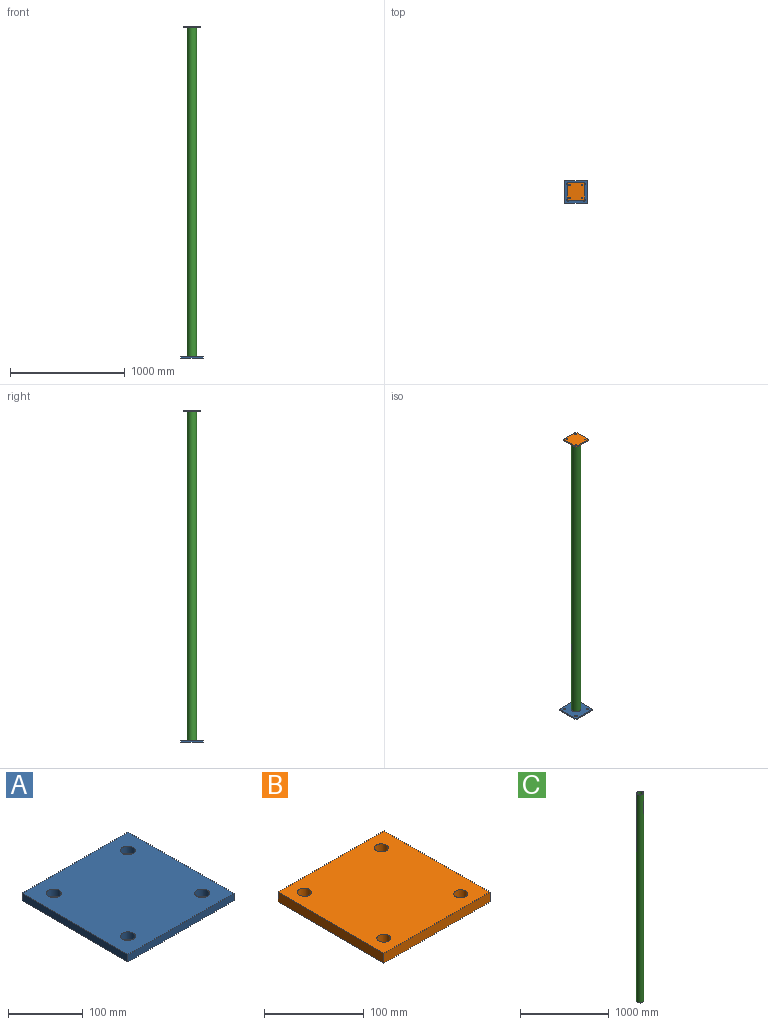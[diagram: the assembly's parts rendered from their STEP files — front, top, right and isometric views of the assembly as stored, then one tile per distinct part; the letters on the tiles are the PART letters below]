
ASSEMBLY  parts=3 mates=2
PART A: 10 faces, bbox 200x200x12 mm
  f0: plane 200x12mm, normal (0,-1,0), area 2400mm2, adj f1,f7,f8,f9
  f1: plane 200x12mm, normal (1,0,0), area 2400mm2, adj f0,f2,f8,f9
  f2: plane 200x12mm, normal (0,1,0), area 2400mm2, adj f1,f7,f8,f9
  f3: cylinder r=10mm len=20mm, axis (0,0,-1), area 754mm2, adj f8,f9
  f4: cylinder r=10mm len=20mm, axis (0,0,-1), area 754mm2, adj f8,f9
  f5: cylinder r=10mm len=20mm, axis (0,0,-1), area 754mm2, adj f8,f9
  f6: cylinder r=10mm len=20mm, axis (0,0,-1), area 754mm2, adj f8,f9
  f7: plane 200x12mm, normal (-1,0,0), area 2400mm2, adj f0,f2,f8,f9
  f8: plane 200x200mm, normal (0,0,1), area 38743.4mm2, adj f0,f1,f2,f3,f4,f5,f6,f7
  f9: plane 200x200mm, normal (0,0,-1), area 38743.4mm2, adj f0,f1,f2,f3,f4,f5,f6,f7
PART B: 10 faces, bbox 150x150x12 mm
  f0: plane 150x12mm, normal (0,-1,0), area 1800mm2, adj f1,f7,f8,f9
  f1: plane 150x12mm, normal (1,0,0), area 1800mm2, adj f0,f2,f8,f9
  f2: plane 150x12mm, normal (0,1,0), area 1800mm2, adj f1,f7,f8,f9
  f3: cylinder r=7mm len=14mm, axis (0,0,-1), area 527.8mm2, adj f8,f9
  f4: cylinder r=7mm len=14mm, axis (0,0,-1), area 527.8mm2, adj f8,f9
  f5: cylinder r=7mm len=14mm, axis (0,0,-1), area 527.8mm2, adj f8,f9
  f6: cylinder r=7mm len=14mm, axis (0,0,-1), area 527.8mm2, adj f8,f9
  f7: plane 150x12mm, normal (-1,0,0), area 1800mm2, adj f0,f2,f8,f9
  f8: plane 150x150mm, normal (0,0,1), area 21884.2mm2, adj f0,f1,f2,f3,f4,f5,f6,f7
  f9: plane 150x150mm, normal (0,0,-1), area 21884.2mm2, adj f0,f1,f2,f3,f4,f5,f6,f7
PART C: 4 faces, bbox 80x80x2864 mm
  f0: cylinder r=35mm len=2864mm, axis (0,0,-1), area 629826.5mm2, adj f2,f3
  f1: cylinder r=40mm len=2864mm, axis (0,0,-1), area 719801.7mm2, adj f2,f3
  f2: plane 80x80mm, normal (0,0,1), area 1178.1mm2, adj f0,f1
  f3: plane 80x80mm, normal (0,0,-1), area 1178.1mm2, adj f0,f1
PLACE A t=(-33.95,-25.64,-15.06)mm
PLACE B t=(-34.01,-25.65,2860.94)mm
PLACE C t=(-33.95,-25.64,-3.06)mm
MATE fastened C.f1 <-> A.f8  axis (0,0,-1) through (-33.95,-25.64,-3.06)mm
MATE fastened B.f9 <-> C.f0  axis (0,0,-1) through (-33.95,-25.64,2860.94)mm
